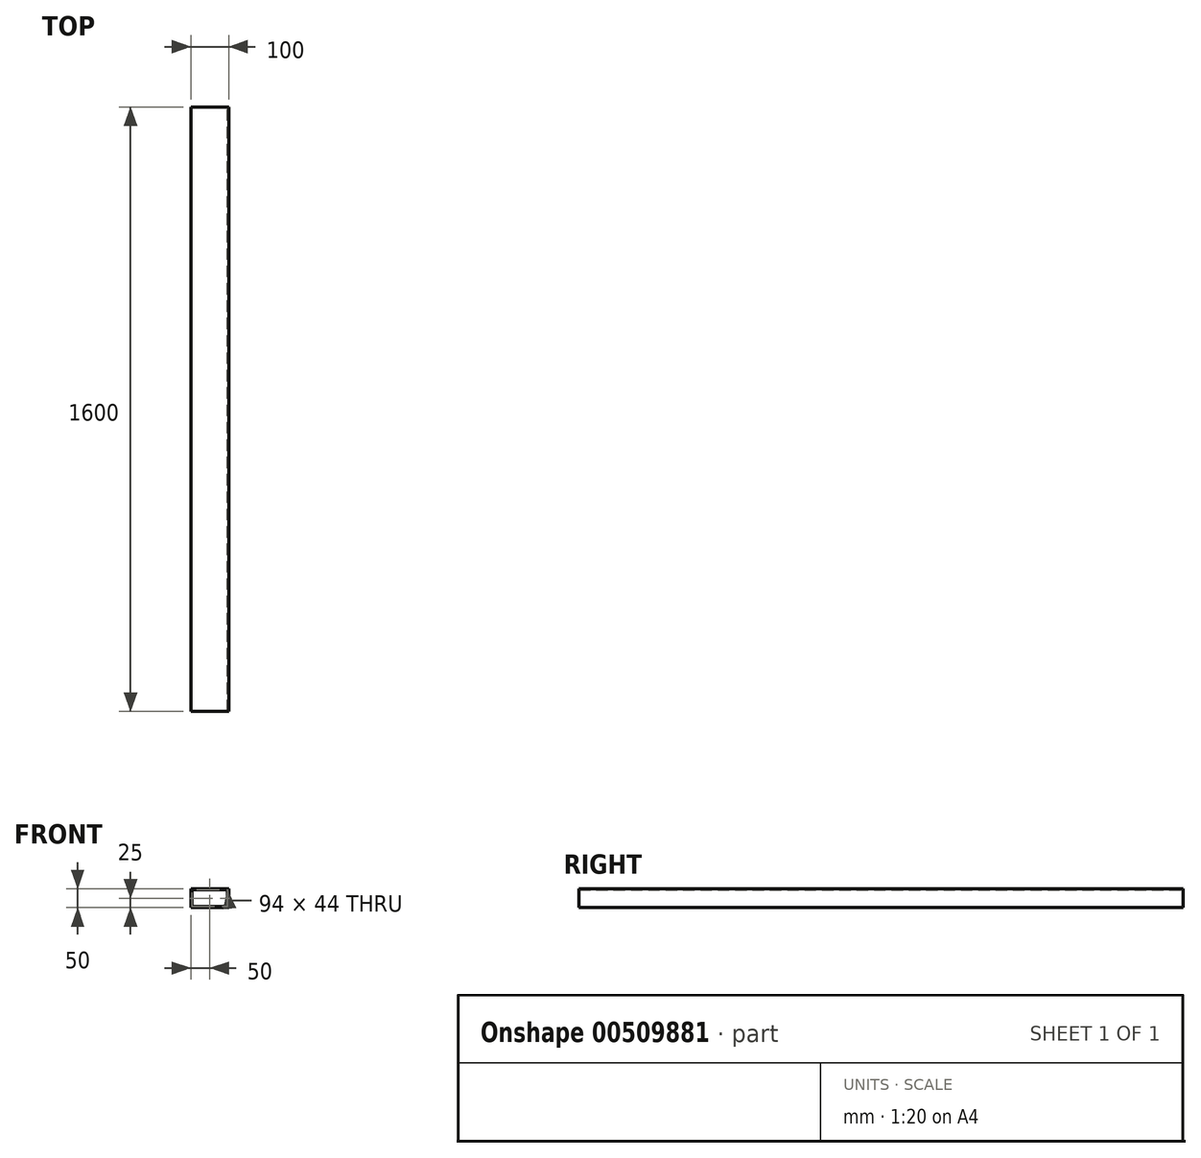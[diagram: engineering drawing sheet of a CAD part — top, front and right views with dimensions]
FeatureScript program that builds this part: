
annotation { "Feature Type Name" : "Feature", "Feature Type Description" : "" }
export const myFeature = defineFeature(function(context is Context, id is Id, definition is map)
    precondition{}
    {
        {
            var Q0;
            Q0=qCreatedBy(makeId("Front.planeOp"),FACE);
            var sketch = newSketch(context, id + "F0", { "sketchPlane" : qUnion([Q0])});
            skLineSegment(sketch, "E0.bottom", {"start": v(50, -25) * mm, "end": v(-50, -25) * mm});
            skLineSegment(sketch, "E0.top", {"start": v(50, 25) * mm, "end": v(-50, 25) * mm});
            skLineSegment(sketch, "E0.left", {"start": v(50, -25) * mm, "end": v(50, 25) * mm});
            skLineSegment(sketch, "E0.right", {"start": v(-50, -25) * mm, "end": v(-50, 25) * mm});
            skPoint(sketch, "E0.middle", {"position": v(0, 0) * mm});
            skLineSegment(sketch, "E1.bottom", {"start": v(47, -22) * mm, "end": v(-47, -22) * mm});
            skLineSegment(sketch, "E1.top", {"start": v(47, 22) * mm, "end": v(-47, 22) * mm});
            skLineSegment(sketch, "E1.left", {"start": v(47, -22) * mm, "end": v(47, 22) * mm});
            skLineSegment(sketch, "E1.right", {"start": v(-47, -22) * mm, "end": v(-47, 22) * mm});
            skSolve(sketch);
        }
        {
            var Q0;
            Q0=makeQuery(id+"F0.imprint","IMPRINT",FACE,{"disambiguationData":[TD([[makeQuery(id+"F0.imprint","IMPRINT",EDGE,{"derivedFrom":sQuery(id+"F0.wireOp",EDGE,"E0.bottom")}),-1.0]])]});
            extrude(context, id + "F1", {"entities" : qUnion([Q0]), "depth" : 1600 * mm, "offsetDistance" : 25 * mm});
        }
    });
